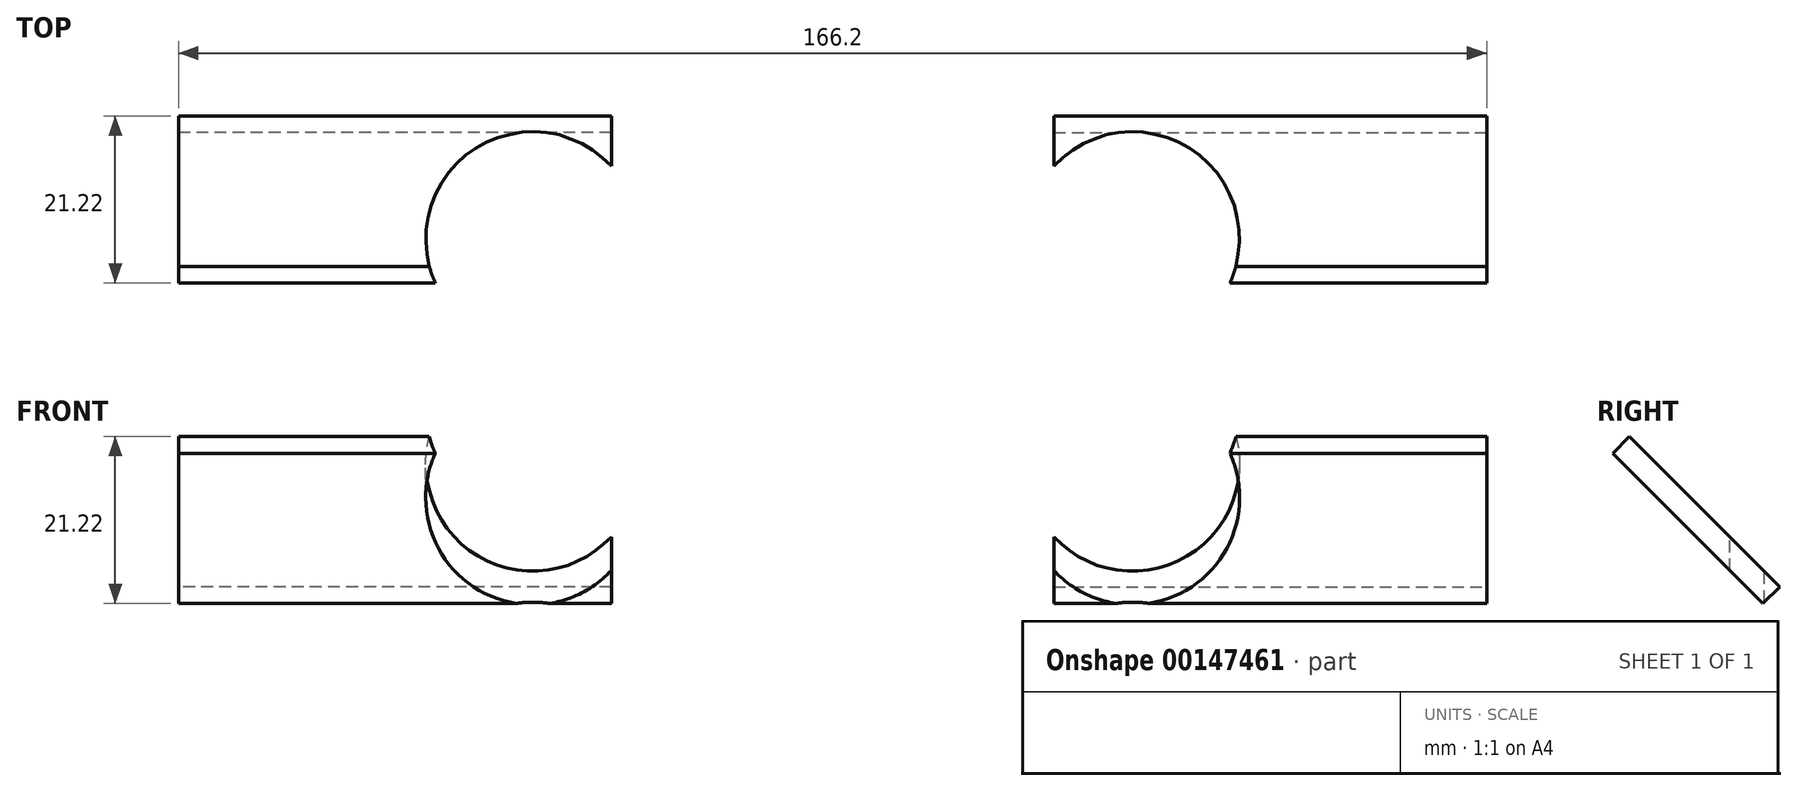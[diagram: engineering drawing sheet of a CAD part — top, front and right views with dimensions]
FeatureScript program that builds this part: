
annotation { "Feature Type Name" : "Feature", "Feature Type Description" : "" }
export const myFeature = defineFeature(function(context is Context, id is Id, definition is map)
    precondition{}
    {
        {
            var Q0;
            Q0=qCreatedBy(makeId("Top.planeOp"),FACE);
            cPlane(context, id + "F0", {"entities" : qUnion([Q0]), "cplaneType" : CPlaneType.OFFSET, "offset" : 26 * mm, "oppositeDirection" : true, "width" : 150 * mm, "height" : 150 * mm});
        }
        {
            var Q0;
            Q0=qCreatedBy(id+"F0.planeOp",FACE);
            cPlane(context, id + "F1", {"entities" : qUnion([Q0]), "cplaneType" : CPlaneType.OFFSET, "offset" : 13.5 * mm, "width" : 150 * mm, "height" : 150 * mm});
        }
        {
            var Q0;
            Q0=qCreatedBy(id+"F1.planeOp",FACE);
            var Q1;
            Q1=qCreatedBy(makeId("Front.planeOp"),FACE);
            cPlane(context, id + "F2", {"entities" : qUnion([Q0, Q1]), "cplaneType" : CPlaneType.MID_PLANE, "offset" : 25 * mm, "width" : 150 * mm, "height" : 150 * mm});
        }
        {
            var Q0;
            Q0=qCreatedBy(makeId("Top.planeOp"),FACE);
            var sketch = newSketch(context, id + "F3", { "sketchPlane" : qUnion([Q0])});
            skPoint(sketch, "E0.middle", {"position": v(-38.1, 0) * mm});
            skPoint(sketch, "E1.orphan", {"position": v(-46.9, 8.41) * mm});
            skPoint(sketch, "E0.left.end.orphan", {"position": v(-49.35, -8.41) * mm});
            skPoint(sketch, "E2.orphan", {"position": v(-29.3, -8.41) * mm});
            skPoint(sketch, "E3.orphan", {"position": v(-26.85, 8.41) * mm});
            skCircle(sketch, "E4", {"center": v(-38.1, 0) * mm, "radius": 13.6 * mm});
            skPoint(sketch, "E5.middle", {"position": v(38.1, 0) * mm});
            skPoint(sketch, "E6.orphan", {"position": v(29.32, 8.41) * mm});
            skPoint(sketch, "E5.left.end.orphan", {"position": v(26.83, -8.41) * mm});
            skPoint(sketch, "E7.orphan", {"position": v(46.88, -8.41) * mm});
            skPoint(sketch, "E8.orphan", {"position": v(49.37, 8.41) * mm});
            skCircle(sketch, "E9", {"center": v(38.1, 0) * mm, "radius": 13.6 * mm});
            skLineSegment(sketch, "E10", {"start": v(-38.1, 0) * mm, "end": v(38.1, 0) * mm});
            skSolve(sketch);
        }
        {
            var Q0;
            Q0=qCreatedBy(id+"F2.planeOp",FACE);
            var sketch = newSketch(context, id + "F4", { "sketchPlane" : qUnion([Q0])});
            skLineSegment(sketch, "E11", {"start": v(38.1, -8.84) * mm, "end": v(-38.1, -8.84) * mm});
            skLineSegment(sketch, "E12", {"start": v(38.1, -8.84) * mm, "end": v(38.1, -0.84) * mm});
            skLineSegment(sketch, "E13", {"start": v(-38.1, -8.84) * mm, "end": v(-38.1, -0.84) * mm});
            skLineSegment(sketch, "E14", {"start": v(38.1, -0.84) * mm, "end": v(28.1, -0.84) * mm});
            skLineSegment(sketch, "E15", {"start": v(-38.1, -0.84) * mm, "end": v(-28.1, -0.84) * mm});
            skLineSegment(sketch, "E16.bottom", {"start": v(28.1, -0.84) * mm, "end": v(83.1, -0.84) * mm});
            skLineSegment(sketch, "E16.top", {"start": v(28.1, -27.84) * mm, "end": v(83.1, -27.84) * mm});
            skLineSegment(sketch, "E16.left", {"start": v(28.1, -0.84) * mm, "end": v(28.1, -27.84) * mm});
            skLineSegment(sketch, "E16.right", {"start": v(83.1, -0.84) * mm, "end": v(83.1, -27.84) * mm});
            skLineSegment(sketch, "E17.bottom", {"start": v(-28.1, -0.84) * mm, "end": v(-83.1, -0.84) * mm});
            skLineSegment(sketch, "E17.top", {"start": v(-28.1, -27.84) * mm, "end": v(-83.1, -27.84) * mm});
            skLineSegment(sketch, "E17.left", {"start": v(-28.1, -0.84) * mm, "end": v(-28.1, -27.84) * mm});
            skLineSegment(sketch, "E17.right", {"start": v(-83.1, -0.84) * mm, "end": v(-83.1, -27.84) * mm});
            skLineSegment(sketch, "E18", {"start": v(0, -8.84) * mm, "end": v(0, 0) * mm});
            skSolve(sketch);
        }
        {
            var Q0;
            Q0=qSketchRegion(id+"F4",true);
            extrude(context, id + "F5", {"entities" : qUnion([Q0]), "depth" : 3 * mm});
        }
        {
            var Q0;
            Q0=qSketchRegion(id+"F3",true);
            extrude(context, id + "F6", {"entities" : qUnion([Q0]), "operationType" : NewBodyOperationType.REMOVE, "oppositeDirection" : true, "depth" : 26 * mm});
        }
    });
